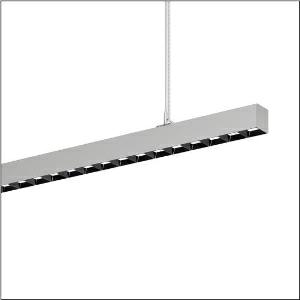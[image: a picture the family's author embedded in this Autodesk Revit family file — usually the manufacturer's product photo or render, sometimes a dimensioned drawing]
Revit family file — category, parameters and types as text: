
# Revit family: silica_r__21_51mx34dc3dsb_1a3f
name_source: partatom
category: Lighting Fixtures
units: mm (PartAtom-declared; Revit-internal decimal feet)

## family parameters
Cut with Voids When Loaded = No
Host = Face
Light Source = No
Part Type = Normal
Room Calculation Point = No
Round Connector Dimension = Use Diameter
Shared = No

## types (1)
- --- (1 x LED, 19200 lm, 129.1 W, 3000K)
    Apparent Load = 129 VA
    CIE Flux Codes = 74 94 99 56 100
    Color Rendering = 80
    Color Temperature = 3000K
    Default Elevation = 1800 mm
    Description = Silica® 21, office luminaire, primary light control with darklight reflector, of PMMA, black, light emission: direct/indirect distribution, primary light characteristic: asymmetric, installation type: suspended mounting, LED, rated luminous flux: 19.200lm, luminous efficacy: 149lm/W, light colour: 830, colour temperature: 3000K, with terminal, 3+2-pole, max. 2.5mm², mains connection: 220..240V, AC, 50/60Hz, rated input power: 129.1W, luminaire housing, of aluminium, metallic grey (RAL 9006), length: 3.004mm, width: 53mm, height: 53mm, protection rating (complete): IP20, insulation class (complete): insulation class I (protective earthing), certification: CE, permissible operating ambient temperature: 0..+35°C, standard: EN 50419, packaging unit: 1 piece
    Height = 53 mm
    Lamp = 1 x LED
    Lamp Light Flux = 19200 lm
    Lamp Power = 129.1 W
    Lamp count = 1
    Length = 3004 mm
    Luminous efficacy = 149 lm/W
    Manufacturer = Siteco
    ModVariant = No
    Model = 51MX34DC3DSB
    Mounting Place = Ceiling
    Mounting Type = Pendant
    Number of Poles = 1
    OnlyDefault = Yes
    Power Factor = 1
    Product Name = Silica® 21
    Product group = office luminaire | ceiling pendant
    ProductGroupID = 902
    Protection Class = Protection class I
    Protection Degree = IP 20
    RLX_Detail_Level = 1
    RLX_Emergency_Light_Flux = 0 lm
    RLX_Emergency_Type = 0
    RLX_Emergency_Type_DB = No
    RlxData = <blob elided: 65353 chars, md5=cdc13a58>
    Socket = socket
    Standby Power = 0 W
    System Light Flux = 19200 lm
    System Power = 129 W
    Type Comments = factory setting: luminous flux: 100 % | dim-lin: 254 | 448 mA
    Type Image = l_1335859.jpg
    URL = http://relux.com
    VarID = @adj_089345
    Voltage = 0 V
    Weight = 0.00 kg
    Width = 53 mm

## geometry (parser evidence)
native form markers: Blend x4, Sweep x10
no freeform markers — native parametric forms only
